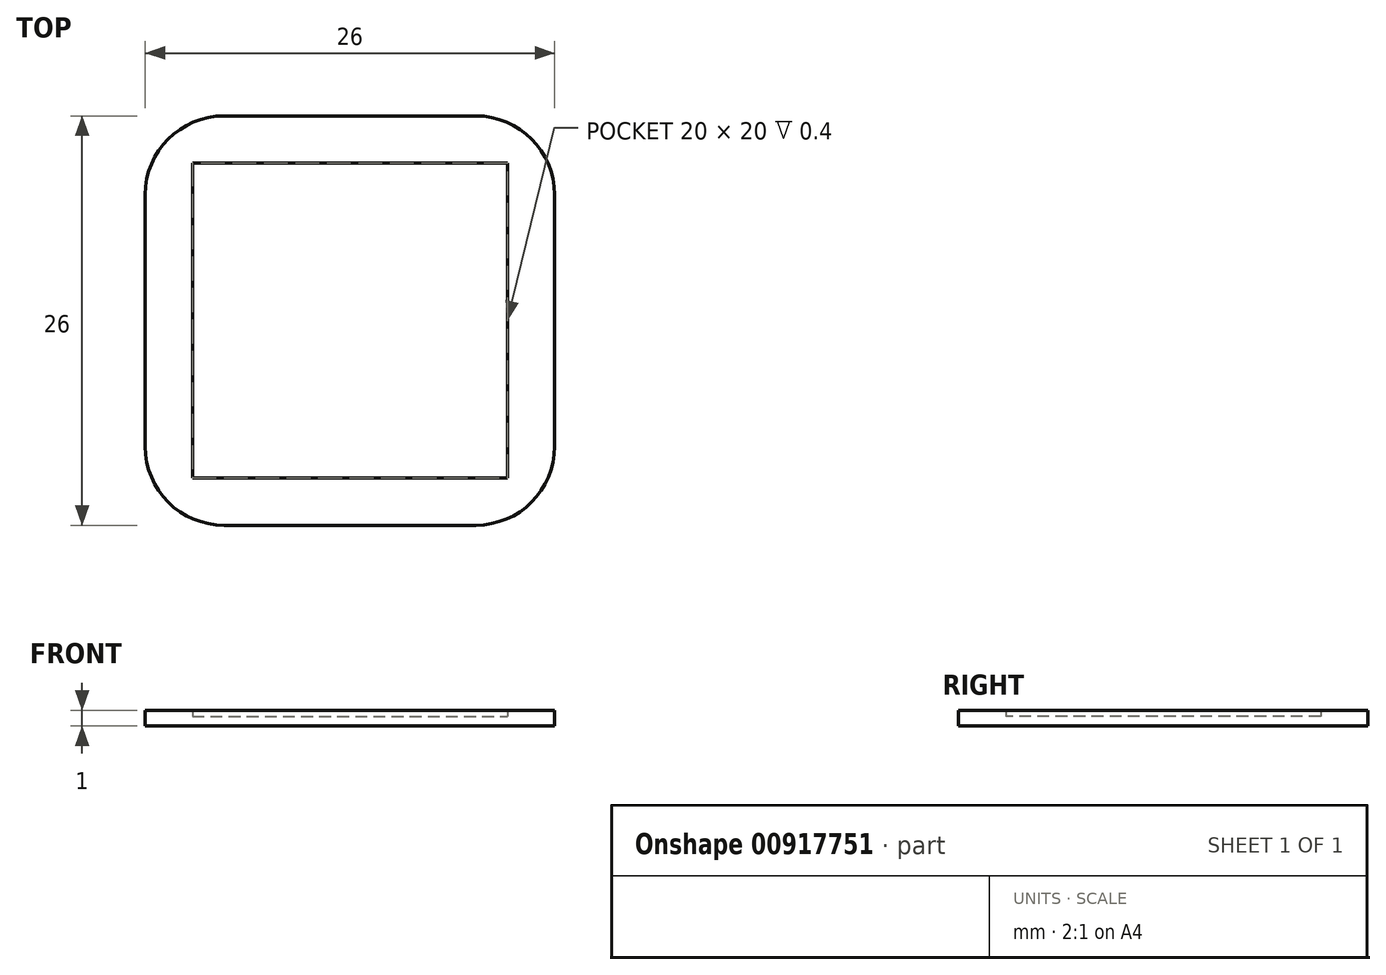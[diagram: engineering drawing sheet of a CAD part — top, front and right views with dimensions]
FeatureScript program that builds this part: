
annotation { "Feature Type Name" : "Feature", "Feature Type Description" : "" }
export const myFeature = defineFeature(function(context is Context, id is Id, definition is map)
    precondition{}
    {
        {
            var Q0;
            Q0=qCreatedBy(makeId("Top.planeOp"),FACE);
            var sketch = newSketch(context, id + "F0", { "sketchPlane" : qUnion([Q0])});
            skLineSegment(sketch, "E0.bottom", {"start": v(11, -11) * mm, "end": v(-11, -11) * mm});
            skLineSegment(sketch, "E0.top", {"start": v(11, 11) * mm, "end": v(-11, 11) * mm});
            skLineSegment(sketch, "E0.left", {"start": v(11, -11) * mm, "end": v(11, 11) * mm});
            skLineSegment(sketch, "E0.right", {"start": v(-11, -11) * mm, "end": v(-11, 11) * mm});
            skPoint(sketch, "E0.middle", {"position": v(0, 0) * mm});
            skSolve(sketch);
        }
        {
            var Q0;
            Q0=makeQuery(id+"F0.imprint","IMPRINT",FACE,{"disambiguationData":[TD([[makeQuery(id+"F0.imprint","IMPRINT",EDGE,{"derivedFrom":sQuery(id+"F0.wireOp",EDGE,"E0.bottom")}),-1.0]])]});
            extrude(context, id + "F1", {"entities" : qUnion([Q0]), "depth" : 0.6 * mm, "offsetDistance" : 25 * mm});
        }
        {
            var Q0;
            Q0=qCreatedBy(makeId("Top.planeOp"),FACE);
            var sketch = newSketch(context, id + "F2", { "sketchPlane" : qUnion([Q0])});
            skLineSegment(sketch, "E1.bottom", {"start": v(10, -10) * mm, "end": v(-10, -10) * mm});
            skLineSegment(sketch, "E1.top", {"start": v(10, 10) * mm, "end": v(-10, 10) * mm});
            skLineSegment(sketch, "E1.left", {"start": v(10, -10) * mm, "end": v(10, 10) * mm});
            skLineSegment(sketch, "E1.right", {"start": v(-10, -10) * mm, "end": v(-10, 10) * mm});
            skPoint(sketch, "E1.middle", {"position": v(0, 0) * mm});
            skLineSegment(sketch, "E2.0", {"start": v(8, 13) * mm, "end": v(-8, 13) * mm});
            skLineSegment(sketch, "E2.1", {"start": v(13, -8) * mm, "end": v(13, 8) * mm});
            skLineSegment(sketch, "E2.2", {"start": v(8, -13) * mm, "end": v(-8, -13) * mm});
            skLineSegment(sketch, "E2.3", {"start": v(-13, -8) * mm, "end": v(-13, 8) * mm});
            skPoint(sketch, "E3.visualSharp", {"position": v(-13, 13) * mm});
            skArc(sketch, "E3.filletArc", {"start": v(-8, 13) * mm, "mid": v(-11.54, 11.54) * mm, "end": v(-13, 8) * mm});
            skPoint(sketch, "E4.visualSharp", {"position": v(13, 13) * mm});
            skArc(sketch, "E4.filletArc", {"start": v(13, 8) * mm, "mid": v(11.54, 11.54) * mm, "end": v(8, 13) * mm});
            skPoint(sketch, "E5.visualSharp", {"position": v(13, -13) * mm});
            skArc(sketch, "E5.filletArc", {"start": v(8, -13) * mm, "mid": v(11.54, -11.54) * mm, "end": v(13, -8) * mm});
            skPoint(sketch, "E6.visualSharp", {"position": v(-13, -13) * mm});
            skArc(sketch, "E6.filletArc", {"start": v(-13, -8) * mm, "mid": v(-11.54, -11.54) * mm, "end": v(-8, -13) * mm});
            skSolve(sketch);
        }
        {
            var Q0;
            Q0=makeQuery(id+"F2.imprint","IMPRINT",FACE,{"disambiguationData":[TD([[makeQuery(id+"F2.imprint","IMPRINT",EDGE,{"derivedFrom":sQuery(id+"F2.wireOp",EDGE,"E1.bottom")}),1.0]])]});
            extrude(context, id + "F3", {"entities" : qUnion([Q0]), "operationType" : NewBodyOperationType.ADD, "depth" : 1 * mm, "offsetDistance" : 25 * mm});
        }
    });
